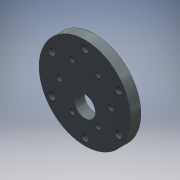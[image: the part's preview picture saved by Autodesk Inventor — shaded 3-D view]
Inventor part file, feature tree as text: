
AUTODESK INVENTOR PART (.ipt)
format: ipt  version: 2016 (Build 200138000, 138)  size: 157,184 bytes
history: native  units: mm
features: extrude x1, sketch x1
ambient origin geometry x8: Origin, YZ Plane, XZ Plane, XY Plane, X Axis, Y Axis, Z Axis, Center Point
bodies: Solid1 (feature_tree)
feature tree (2):
  extrude  "Extrusion1"  Depth=6.0mm
  sketch  "Sketch1"  dims[d0=55.0mm d1=12.5mm d2=7.0mm d3=3.2mm d4=15.5mm d5=60.0mm d7=360.0deg d9=4.2mm d10=23.0mm d11=60.0mm d13=360.0deg d15=6.0mm d16=0.0mm]
